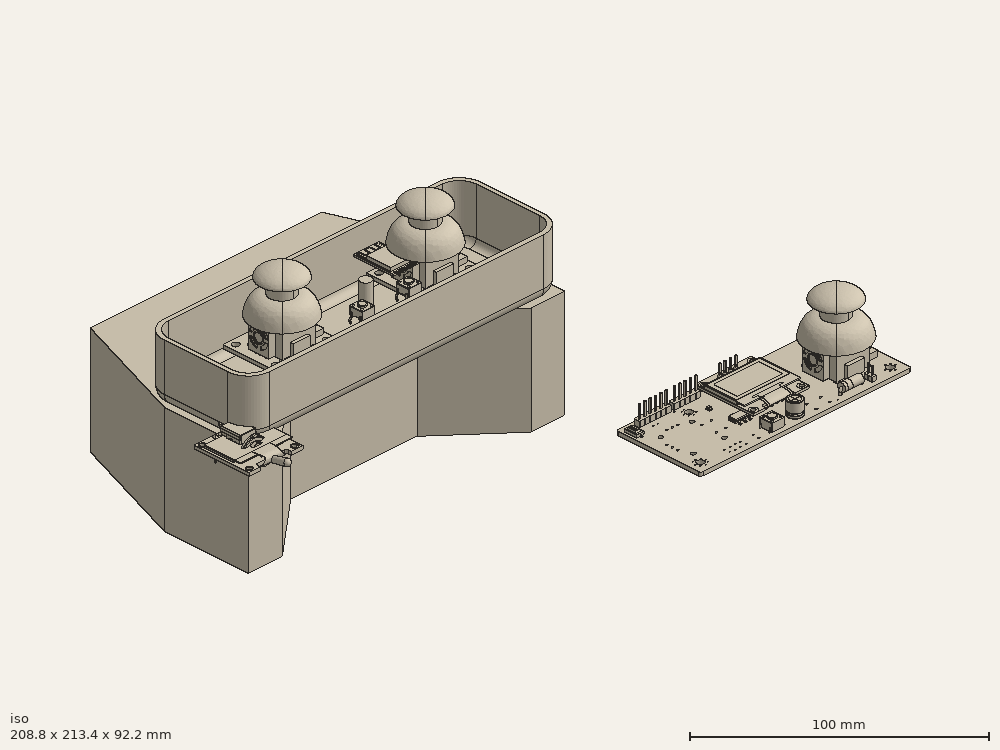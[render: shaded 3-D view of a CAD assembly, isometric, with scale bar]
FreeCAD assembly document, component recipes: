
FREECAD ASSEMBLY — COMPONENT RECIPES ("Transmitter Case V1")

This assembly document has 8 components, labeled P0..P7 below (a component is one placed body or linked part). 4 of them carry a construction recipe — the FreeCAD feature program that regenerates the part from scratch, quoted from this document or its linked companion documents; the rest are supplied as boundary geometry only. No exploded tour is included for this assembly.
COMPONENT P0 — geometry summary ("TransmitterV1"; no construction recipe available for this part):
  bounding box: 100.0 x 40.4 x 40.3 mm
  tessellated surface: 126,652 triangles
  volume: 22622 mm^3 (14% of its bounding box)
COMPONENT P1 — recipe-attached ("Body", modeled in this document).
Construction recipe (the document's own serialized feature program — sketch geometry with constraints, then the solid features built on it; lengths are millimeters unless a unit is written):

FEATURE [Sketcher::SketchObject] Sketch
  FullyConstrained = true
  MapMode = 5
  Support = -> [XY_Plane]
  sketch-geometry (14):
    g0: LineSegment StartX=0 StartY=0 StartZ=0 EndX=0 EndY=40 EndZ=0
    g1: LineSegment StartX=0 StartY=40 StartZ=0 EndX=20 EndY=95 EndZ=0
    g2: LineSegment StartX=20 StartY=95 StartZ=0 EndX=130 EndY=95 EndZ=0
    g3: LineSegment StartX=130 StartY=95 StartZ=0 EndX=150 EndY=40 EndZ=0
    g4: LineSegment StartX=150 StartY=40 StartZ=0 EndX=150 EndY=0 EndZ=0
    g5: LineSegment StartX=150 StartY=0 StartZ=0 EndX=134 EndY=0 EndZ=0
    g6: LineSegment StartX=134 StartY=0 StartZ=0 EndX=105 EndY=25 EndZ=0
    g7: LineSegment StartX=105 StartY=25 StartZ=0 EndX=45 EndY=25 EndZ=0
    g8: LineSegment StartX=45 StartY=25 StartZ=0 EndX=16 EndY=0 EndZ=0
    g9: LineSegment StartX=16 StartY=0 StartZ=0 EndX=0 EndY=0 EndZ=0
    g10: LineSegment StartX=0 StartY=40 StartZ=0 EndX=20 EndY=40 EndZ=0
    g11: LineSegment StartX=150 StartY=40 StartZ=0 EndX=130 EndY=40 EndZ=0
    g12: LineSegment StartX=134 StartY=0 StartZ=0 EndX=105 EndY=0 EndZ=0
    g13: LineSegment StartX=16 StartY=0 StartZ=0 EndX=45 EndY=0 EndZ=0
  constraints (41):
    c: Coincident(g0,g-1)
    c: PointOnObject(g0,g-2)
    c: Coincident(g1,g0)
    c: Horizontal(g2)
    c: Coincident(g4,g3)
    c: Vertical(g4)
    c: Horizontal(g5)
    c: Coincident(g6,g5)
    c: Coincident(g7,g6)
    c: Horizontal(g7)
    c: Coincident(g8,g7)
    c: PointOnObject(g8,g-1)
    c: Coincident(g9,g8)
    c: Coincident(g9,g0)
    c: PointOnObject(g5,g-1)
    c: Equal(g0,g4)
    c: Equal(g8,g6)
    c: Equal(g9,g5)
    c: Equal(g1,g3)
    c: Coincident(g10,g0)
    c: Horizontal(g10)
    c: Coincident(g11,g3)
    c: Horizontal(g11)
    c: Coincident(g12,g5)
    c: Coincident(g13,g8)
    c: Horizontal(g13)
    c: Horizontal(g12)
    c: Vertical(g13,g7)
    c: Vertical(g12,g6)
    c: Distance(g7) = 60
    c: Distance(g3,g1) = 110
    c: Equal(g10,g11)
    c: DistanceY(g0,g2) = 95
    c: Distance(g0,g5) = 150
    c: Coincident(g1,g2)
    c: Coincident(g2,g3)
    c: Vertical(g11,g2)
    c: Coincident(g5,g4)
    c: Distance(g4) = 40
    c: Distance(g5) = 16
    c: Distance(g7,g13) = 25
FEATURE [PartDesign::Pad] Pad
  Direction = (1,1,1)
  Length = 48
  Length2 = 100
  Profile = -> Sketch
  Reversed = true
  Type = 0
FEATURE [Sketcher::SketchObject] Sketch001
  ExternalGeometry = -> [Pad]
  FullyConstrained = true
  MapMode = 5
  Support = -> [Pad]
  sketch-geometry (4):
    g0: LineSegment StartX=0 StartY=-1 StartZ=0 EndX=-63.05 EndY=-1 EndZ=0
    g1: LineSegment StartX=-63.05 StartY=-1 StartZ=0 EndX=-63.05 EndY=98.76 EndZ=0
    g2: LineSegment StartX=-63.05 StartY=98.76 StartZ=0 EndX=0 EndY=98.76 EndZ=0
    g3: LineSegment StartX=0 StartY=98.76 StartZ=0 EndX=0 EndY=-1 EndZ=0
  constraints (12):
    c: Coincident(g0,g1)
    c: Coincident(g1,g2)
    c: Coincident(g2,g3)
    c: Coincident(g3,g0)
    c: Horizontal(g0)
    c: Horizontal(g2)
    c: Vertical(g1)
    c: Vertical(g3)
    c: Distance(g0) = 63.05
    c: Distance(g3) = 99.76
    c: Vertical(g-1,g0)
    c: Distance(g-1,g0) = 1
FEATURE [PartDesign::Body] Body
  Group = -> [Sketch,Pad,Sketch001]
  Origin = -> Origin
  Tip = -> Pad
COMPONENT P2 — recipe-attached ("Body001", modeled in this document).
Construction recipe (the document's own serialized feature program — sketch geometry with constraints, then the solid features built on it; lengths are millimeters unless a unit is written):

FEATURE [Sketcher::SketchObject] Sketch002
  FullyConstrained = true
  MapMode = 5
  Support = -> [XY_Plane001]
  sketch-geometry (16):
    g0: LineSegment StartX=10 StartY=0 StartZ=0 EndX=140 EndY=0 EndZ=0
    g1: LineSegment StartX=150 StartY=10 StartZ=0 EndX=150 EndY=40 EndZ=0
    g2: LineSegment StartX=140 StartY=50 StartZ=0 EndX=10 EndY=50 EndZ=0
    g3: LineSegment StartX=0 StartY=40 StartZ=0 EndX=0 EndY=10 EndZ=0
    g4: LineSegment StartX=0 StartY=0 StartZ=0 EndX=150 EndY=0 EndZ=0
    g5: LineSegment StartX=150 StartY=0 StartZ=0 EndX=150 EndY=50 EndZ=0
    g6: LineSegment StartX=150 StartY=50 StartZ=0 EndX=0 EndY=50 EndZ=0
    g7: LineSegment StartX=0 StartY=50 StartZ=0 EndX=0 EndY=0 EndZ=0
    g8: ArcOfCircle CenterX=140 CenterY=40 CenterZ=0 NormalX=0 NormalY=0 NormalZ=1 AngleXU=0 Radius=10 StartAngle=2e-16 EndAngle=1.5708
    g9: ArcOfCircle CenterX=140 CenterY=10 CenterZ=0 NormalX=0 NormalY=0 NormalZ=1 AngleXU=0 Radius=10 StartAngle=4.71239 EndAngle=6.28319
    g10: ArcOfCircle CenterX=10 CenterY=10 CenterZ=0 NormalX=0 NormalY=0 NormalZ=1 AngleXU=0 Radius=10 StartAngle=3.14159 EndAngle=4.71239
    g11: ArcOfCircle CenterX=10 CenterY=40 CenterZ=0 NormalX=0 NormalY=0 NormalZ=1 AngleXU=0 Radius=10 StartAngle=1.5708 EndAngle=3.14159
    g12: LineSegment StartX=140 StartY=40 StartZ=0 EndX=140 EndY=50 EndZ=0
    g13: LineSegment StartX=140 StartY=10 StartZ=0 EndX=140 EndY=0 EndZ=0
    g14: LineSegment StartX=10 StartY=0 StartZ=0 EndX=10 EndY=10 EndZ=0
    g15: LineSegment StartX=10 StartY=40 StartZ=0 EndX=10 EndY=50 EndZ=0
  constraints (39):
    c: Horizontal(g0)
    c: Vertical(g1)
    c: Vertical(g3)
    c: Coincident(g4,g5)
    c: Coincident(g5,g6)
    c: Coincident(g6,g7)
    c: Coincident(g7,g4)
    c: Horizontal(g4)
    c: Horizontal(g6)
    c: Vertical(g5)
    c: Vertical(g7)
    c: Coincident(g4,g-1)
    c: Distance(g5) = 50
    c: Distance(g4) = 150
    c: Tangent(g2,g8) = -1.5708
    c: Tangent(g1,g8) = -1.5708
    c: Tangent(g1,g9) = -1.5708
    c: Tangent(g0,g9) = -1.5708
    c: Tangent(g0,g10) = -1.5708
    c: Tangent(g3,g10) = -1.5708
    c: Tangent(g2,g11) = -1.5708
    c: Tangent(g3,g11) = -1.5708
    c: PointOnObject(g0,g4)
    c: PointOnObject(g3,g7)
    c: PointOnObject(g2,g6)
    c: PointOnObject(g1,g5)
    c: Coincident(g12,g8)
    c: Coincident(g12,g2)
    c: Vertical(g12)
    c: Coincident(g13,g9)
    c: Coincident(g13,g0)
    c: Coincident(g14,g0)
    c: Coincident(g14,g10)
    c: Coincident(g15,g11)
    c: Coincident(g15,g2)
    c: Equal(g15,g14)
    c: Equal(g14,g12)
    c: Equal(g12,g13)
    c: Distance(g15) = 10
FEATURE [PartDesign::Pad] Pad001
  Direction = (1,1,1)
  Length = 26
  Length2 = 100
  Profile = -> Sketch002
  Type = 0
FEATURE [PartDesign::Fillet] Fillet
  Base = -> Pad001 [Edge3]
  BaseFeature = -> Pad001
  Radius = 5
  SupportTransform = false
FEATURE [PartDesign::Thickness] Thickness
  Base = -> Fillet [Face4]
  BaseFeature = -> Fillet
  Intersection = false
  Join = 0
  Mode = 0
  Reversed = true
  SupportTransform = false
  Value = 2
FEATURE [Sketcher::SketchObject] Sketch010
  ExternalGeometry = -> [Thickness]
  FullyConstrained = true
  MapMode = 5
  Placement = pos=(0,0,2) rot=(0,0,1;0rad)
  Support = -> [Thickness]
  sketch-geometry (4):
    g0: Circle CenterX=52 CenterY=37.5 CenterZ=0 NormalX=0 NormalY=0 NormalZ=1 AngleXU=0 Radius=2.5
    g1: Circle CenterX=92.5 CenterY=36.8 CenterZ=0 NormalX=0 NormalY=0 NormalZ=1 AngleXU=0 Radius=2.5
    g2: Circle CenterX=121 CenterY=11.2 CenterZ=0 NormalX=0 NormalY=0 NormalZ=1 AngleXU=0 Radius=2.5
    g3: Circle CenterX=31 CenterY=11.2 CenterZ=0 NormalX=0 NormalY=0 NormalZ=1 AngleXU=0 Radius=2.5
  constraints (12):
    c: Diameter(g3) = 5
    c: Equal(g3,g0)
    c: Equal(g3,g1)
    c: Equal(g3,g2)
    c: Distance(g3,g-6) = 11.2
    c: Distance(g3,g-4) = 31
    c: Distance(g2,g-6) = 11.2
    c: Distance(g2,g-5) = 29
    c: Distance(g0,g-3) = 12.5
    c: Distance(g0,g-4) = 52
    c: Distance(g1,g-3) = 13.2
    c: Distance(g1,g-5) = 57.5
FEATURE [PartDesign::Pad] Pad004
  BaseFeature = -> Thickness
  Direction = (1,1,1)
  Length = 11
  Length2 = 100
  Profile = -> Sketch010
  Type = 0
FEATURE [Sketcher::SketchObject] Sketch011
  ExternalGeometry = -> [Pad004]
  FullyConstrained = false
  MapMode = 5
  Placement = pos=(-1.1e-14,50,0) rot=(0,0.707107,0.707107;3.14159rad)
  Support = -> [Pad004]
  sketch-geometry (2):
    g0: Circle CenterX=-134.032 CenterY=16.8099 CenterZ=0 NormalX=0 NormalY=0 NormalZ=1 AngleXU=0 Radius=3.5
    g1: Circle CenterX=-15.9615 CenterY=16.8655 CenterZ=0 NormalX=0 NormalY=0 NormalZ=1 AngleXU=0 Radius=3.5
  constraints (4):
    c: Distance(g-4) = 21
    c: Distance(g-4) = 21
    c: Diameter(g0) = 7
    c: Equal(g0,g1)
FEATURE [PartDesign::Body] Body001
  Group = -> [Sketch002,Pad001,Fillet,Thickness,Sketch010,Pad004,Sketch011]
  Origin = -> Origin001
  Tip = -> Pad004
COMPONENT P3 — recipe-attached ("Body002", modeled in this document).
Construction recipe (the document's own serialized feature program — sketch geometry with constraints, then the solid features built on it; lengths are millimeters unless a unit is written):

FEATURE [Sketcher::SketchObject] Sketch003
  FullyConstrained = true
  MapMode = 5
  Support = -> [XY_Plane009]
  sketch-geometry (40):
    g0: LineSegment StartX=0 StartY=0 StartZ=0 EndX=30 EndY=0 EndZ=0
    g1: LineSegment StartX=30 StartY=0 StartZ=0 EndX=30 EndY=25 EndZ=0
    g2: LineSegment StartX=30 StartY=25 StartZ=0 EndX=0 EndY=25 EndZ=0
    g3: LineSegment StartX=0 StartY=25 StartZ=0 EndX=0 EndY=0 EndZ=0
    g4: Circle CenterX=4.4 CenterY=8.5 CenterZ=0 NormalX=0 NormalY=0 NormalZ=1 AngleXU=0 Radius=0.75
    g5: Circle CenterX=4.4 CenterY=11.05 CenterZ=0 NormalX=0 NormalY=0 NormalZ=1 AngleXU=0 Radius=0.75
    g6: Circle CenterX=4.4 CenterY=13.6 CenterZ=0 NormalX=0 NormalY=0 NormalZ=1 AngleXU=0 Radius=0.75
    g7: Circle CenterX=11.4 CenterY=20.6 CenterZ=0 NormalX=0 NormalY=0 NormalZ=1 AngleXU=0 Radius=0.75
    g8: Circle CenterX=13.95 CenterY=20.6 CenterZ=0 NormalX=0 NormalY=0 NormalZ=1 AngleXU=0 Radius=0.75
    g9: Circle CenterX=16.5 CenterY=20.6 CenterZ=0 NormalX=0 NormalY=0 NormalZ=1 AngleXU=0 Radius=0.75
    g10: Circle CenterX=26.4 CenterY=14.65 CenterZ=0 NormalX=0 NormalY=0 NormalZ=1 AngleXU=0 Radius=0.75
    g11: Circle CenterX=26.4 CenterY=7.8 CenterZ=0 NormalX=0 NormalY=0 NormalZ=1 AngleXU=0 Radius=0.75
    g12: Circle CenterX=22.1 CenterY=7.8 CenterZ=0 NormalX=0 NormalY=0 NormalZ=1 AngleXU=0 Radius=0.75
    g13: Circle CenterX=22.1 CenterY=14.65 CenterZ=0 NormalX=0 NormalY=0 NormalZ=1 AngleXU=0 Radius=0.75
    g14: Circle CenterX=6.5 CenterY=3.35 CenterZ=0 NormalX=0 NormalY=0 NormalZ=1 AngleXU=0 Radius=1
    g15: Circle CenterX=6.5 CenterY=18.75 CenterZ=0 NormalX=0 NormalY=0 NormalZ=1 AngleXU=0 Radius=1
    g16: Circle CenterX=21.35 CenterY=3.35 CenterZ=0 NormalX=0 NormalY=0 NormalZ=1 AngleXU=0 Radius=1
    g17: Circle CenterX=21.35 CenterY=18.75 CenterZ=0 NormalX=0 NormalY=0 NormalZ=1 AngleXU=0 Radius=1
    g18: LineSegment StartX=13.95 StartY=20.6 StartZ=0 EndX=13.95 EndY=25 EndZ=0
    g19: LineSegment StartX=16.5 StartY=20.6 StartZ=0 EndX=13.95 EndY=20.6 EndZ=0
    g20: LineSegment StartX=11.4 StartY=20.6 StartZ=0 EndX=13.95 EndY=20.6 EndZ=0
    g21: LineSegment StartX=13.95 StartY=20.6 StartZ=0 EndX=0 EndY=20.6 EndZ=0
    g22: LineSegment StartX=4.4 StartY=11.05 StartZ=0 EndX=0 EndY=11.05 EndZ=0
    g23: LineSegment StartX=4.4 StartY=13.6 StartZ=0 EndX=4.4 EndY=11.05 EndZ=0
    g24: LineSegment StartX=4.4 StartY=11.05 StartZ=0 EndX=4.4 EndY=8.5 EndZ=0
    g25: LineSegment StartX=4.4 StartY=11.05 StartZ=0 EndX=4.4 EndY=25 EndZ=0
    g26: LineSegment StartX=6.5 StartY=3.35 StartZ=0 EndX=0 EndY=3.35 EndZ=0
    g27: LineSegment StartX=6.5 StartY=3.35 StartZ=0 EndX=6.5 EndY=0 EndZ=0
    g28: LineSegment StartX=26.4 StartY=7.8 StartZ=0 EndX=26.4 EndY=0 EndZ=0
    g29: LineSegment StartX=26.4 StartY=7.8 StartZ=0 EndX=30 EndY=7.8 EndZ=0
    g30: LineSegment StartX=6.5 StartY=18.75 StartZ=0 EndX=6.5 EndY=25 EndZ=0
    g31: LineSegment StartX=6.5 StartY=18.75 StartZ=0 EndX=0 EndY=18.75 EndZ=0
    g32: LineSegment StartX=21.35 StartY=18.75 StartZ=0 EndX=21.35 EndY=25 EndZ=0
    g33: LineSegment StartX=21.35 StartY=18.75 StartZ=0 EndX=30 EndY=18.75 EndZ=0
    g34: LineSegment StartX=21.35 StartY=3.35 StartZ=0 EndX=21.35 EndY=0 EndZ=0
    g35: LineSegment StartX=21.35 StartY=3.35 StartZ=0 EndX=30 EndY=3.35 EndZ=0
    g36: LineSegment StartX=26.4 StartY=14.65 StartZ=0 EndX=26.4 EndY=7.8 EndZ=0
    g37: LineSegment StartX=26.4 StartY=7.8 StartZ=0 EndX=22.1 EndY=7.8 EndZ=0
    g38: LineSegment StartX=22.1 StartY=14.65 StartZ=0 EndX=22.1 EndY=7.8 EndZ=0
    g39: LineSegment StartX=26.4 StartY=14.65 StartZ=0 EndX=22.1 EndY=14.65 EndZ=0
  constraints (111):
    c: Coincident(g0,g1)
    c: Coincident(g1,g2)
    c: Coincident(g2,g3)
    c: Coincident(g3,g0)
    c: Horizontal(g0)
    c: Horizontal(g2)
    c: Vertical(g1)
    c: Vertical(g3)
    c: Coincident(g0,g-1)
    c: Distance(g2) = 30
    c: Distance(g1) = 25
    c: Diameter(g4) = 1.5
    c: Equal(g4,g5) = 1.5
    c: Equal(g4,g6) = 1.5
    c: Equal(g4,g7) = 1.5
    c: Equal(g4,g8) = 1.5
    c: Equal(g4,g9) = 1.5
    c: Equal(g4,g10) = 1.5
    c: Equal(g4,g11) = 1.5
    c: Equal(g4,g12) = 1.5
    c: Diameter(g14) = 2
    c: Equal(g14,g15) = 2
    c: Equal(g14,g16) = 2
    c: Equal(g14,g17) = 2
    c: Coincident(g18,g8)
    c: Vertical(g18)
    c: Coincident(g19,g9)
    c: Coincident(g19,g8)
    c: Horizontal(g19)
    c: Coincident(g20,g7)
    c: Coincident(g20,g8)
    c: Horizontal(g20)
    c: Equal(g20,g19)
    c: Distance(g18) = 4.4
    c: Coincident(g21,g8)
    c: PointOnObject(g21,g3)
    c: Horizontal(g21)
    c: PointOnObject(g18,g2)
    c: Distance(g21) = 13.95
    c: Distance(g20) = 2.55
    c: Coincident(g22,g5)
    c: PointOnObject(g22,g-2)
    c: Horizontal(g22)
    c: Coincident(g23,g6)
    c: Coincident(g23,g5)
    c: Vertical(g23)
    c: Coincident(g24,g5)
    c: Coincident(g24,g4)
    c: Vertical(g24)
    c: Equal(g24,g23)
    c: Distance(g22) = 4.4
    c: Coincident(g25,g5)
    c: PointOnObject(g25,g2)
    c: Vertical(g25)
    c: Distance(g25) = 13.95
    c: Distance(g24) = 2.55
    c: Coincident(g26,g14)
    c: PointOnObject(g26,g-2)
    c: Horizontal(g26)
    c: Coincident(g27,g14)
    c: PointOnObject(g27,g0)
    c: Vertical(g27)
    c: Coincident(g28,g11)
    c: PointOnObject(g28,g0)
    c: Vertical(g28)
    c: Coincident(g29,g11)
    c: Horizontal(g29)
    c: Coincident(g30,g15)
    c: PointOnObject(g30,g2)
    c: Vertical(g30)
    c: Coincident(g31,g15)
    c: PointOnObject(g31,g3)
    c: Horizontal(g31)
    c: Coincident(g32,g17)
    c: PointOnObject(g32,g2)
    c: Vertical(g32)
    c: Coincident(g33,g17)
    c: PointOnObject(g33,g1)
    c: Horizontal(g33)
    c: Coincident(g34,g16)
    c: PointOnObject(g34,g0)
    c: Vertical(g34)
    c: Coincident(g35,g16)
    c: PointOnObject(g35,g1)
    c: Horizontal(g35)
    c: Coincident(g36,g10)
    c: Coincident(g36,g11)
    c: Vertical(g36)
    c: Coincident(g37,g11)
    c: Coincident(g37,g12)
    c: Horizontal(g37)
    c: Coincident(g38,g13)
    c: Coincident(g38,g12)
    c: Vertical(g38)
    c: Coincident(g39,g10)
    c: Coincident(g39,g13)
    c: Horizontal(g39)
    c: Distance(g29) = 3.6
    c: Distance(g37) = 4.3
    c: Distance(g38) = 6.85
    c: Distance(g28) = 7.8
    c: PointOnObject(g29,g1)
    c: Equal(g13,g12)
    c: Distance(g31) = 6.5
    c: Distance(g30) = 6.25
    c: Distance(g32) = 6.25
    c: Distance(g33) = 8.65
    c: Distance(g35) = 8.65
    c: Distance(g34) = 3.35
    c: Distance(g27) = 3.35
    c: Distance(g26) = 6.5
FEATURE [PartDesign::Pad] Pad002
  Direction = (1,1,1)
  Length = 1.6
  Length2 = 100
  Profile = -> Sketch003
  Type = 0
FEATURE [Sketcher::SketchObject] Sketch004
  ExternalGeometry = -> [Pad002]
  FullyConstrained = true
  MapMode = 5
  Placement = pos=(0,0,1.6) rot=(0,0,1;0rad)
  Support = -> [Pad002]
  sketch-geometry (4):
    g0: Circle CenterX=27 CenterY=22 CenterZ=0 NormalX=0 NormalY=0 NormalZ=1 AngleXU=0 Radius=1.55
    g1: Circle CenterX=3 CenterY=22 CenterZ=0 NormalX=0 NormalY=0 NormalZ=1 AngleXU=0 Radius=1.55
    g2: Circle CenterX=27 CenterY=3 CenterZ=0 NormalX=0 NormalY=0 NormalZ=1 AngleXU=0 Radius=1.55
    g3: Circle CenterX=3 CenterY=3 CenterZ=0 NormalX=0 NormalY=0 NormalZ=1 AngleXU=0 Radius=1.55
  constraints (12):
    c: Diameter(g0) = 3.1
    c: Equal(g0,g1) = 3.1
    c: Equal(g0,g2) = 3.1
    c: Equal(g0,g3) = 3.1
    c: Distance(g2,g-5) = 3
    c: Distance(g2,g-6) = 3
    c: Distance(g0,g-3) = 3
    c: Distance(g0,g-5) = 3
    c: Distance(g1,g-3) = 3
    c: Distance(g1,g-4) = 3
    c: Distance(g3,g-4) = 3
    c: Distance(g3,g-6) = 3
FEATURE [PartDesign::Pocket] Pocket
  BaseFeature = -> Pad002
  Length = 5
  Length2 = 100
  Profile = -> Sketch004
  Type = 0
FEATURE [Sketcher::SketchObject] Sketch008
  FullyConstrained = true
  MapMode = 5
  Support = -> [XY_Plane009]
FEATURE [Sketcher::SketchObject] Sketch009
  FullyConstrained = true
  MapMode = 5
  Support = -> [XY_Plane009]
FEATURE [PartDesign::Body] Body002
  Group = -> [Sketch003,Pad002,Sketch004,Pocket,Sketch008,Sketch009]
  Origin = -> Origin009
  Placement = pos=(27,14,12) rot=(0,0,1;0rad)
  Tip = -> Pocket
COMPONENT P4 — recipe-attached ("Body003", modeled in this document).
Construction recipe (the document's own serialized feature program — sketch geometry with constraints, then the solid features built on it; lengths are millimeters unless a unit is written):

FEATURE [Sketcher::SketchObject] Sketch006
  FullyConstrained = true
  MapMode = 5
  Support = -> [XY_Plane010]
  sketch-geometry (40):
    g0: LineSegment StartX=0 StartY=0 StartZ=0 EndX=30 EndY=0 EndZ=0
    g1: LineSegment StartX=30 StartY=0 StartZ=0 EndX=30 EndY=25 EndZ=0
    g2: LineSegment StartX=30 StartY=25 StartZ=0 EndX=0 EndY=25 EndZ=0
    g3: LineSegment StartX=0 StartY=25 StartZ=0 EndX=0 EndY=0 EndZ=0
    g4: Circle CenterX=4.4 CenterY=8.5 CenterZ=0 NormalX=0 NormalY=0 NormalZ=1 AngleXU=0 Radius=0.75
    g5: Circle CenterX=4.4 CenterY=11.05 CenterZ=0 NormalX=0 NormalY=0 NormalZ=1 AngleXU=0 Radius=0.75
    g6: Circle CenterX=4.4 CenterY=13.6 CenterZ=0 NormalX=0 NormalY=0 NormalZ=1 AngleXU=0 Radius=0.75
    g7: Circle CenterX=11.4 CenterY=20.6 CenterZ=0 NormalX=0 NormalY=0 NormalZ=1 AngleXU=0 Radius=0.75
    g8: Circle CenterX=13.95 CenterY=20.6 CenterZ=0 NormalX=0 NormalY=0 NormalZ=1 AngleXU=0 Radius=0.75
    g9: Circle CenterX=16.5 CenterY=20.6 CenterZ=0 NormalX=0 NormalY=0 NormalZ=1 AngleXU=0 Radius=0.75
    g10: Circle CenterX=26.4 CenterY=14.65 CenterZ=0 NormalX=0 NormalY=0 NormalZ=1 AngleXU=0 Radius=0.75
    g11: Circle CenterX=26.4 CenterY=7.8 CenterZ=0 NormalX=0 NormalY=0 NormalZ=1 AngleXU=0 Radius=0.75
    g12: Circle CenterX=22.1 CenterY=7.8 CenterZ=0 NormalX=0 NormalY=0 NormalZ=1 AngleXU=0 Radius=0.75
    g13: Circle CenterX=22.1 CenterY=14.65 CenterZ=0 NormalX=0 NormalY=0 NormalZ=1 AngleXU=0 Radius=0.75
    g14: Circle CenterX=6.5 CenterY=3.35 CenterZ=0 NormalX=0 NormalY=0 NormalZ=1 AngleXU=0 Radius=1
    g15: Circle CenterX=6.5 CenterY=18.75 CenterZ=0 NormalX=0 NormalY=0 NormalZ=1 AngleXU=0 Radius=1
    g16: Circle CenterX=21.35 CenterY=3.35 CenterZ=0 NormalX=0 NormalY=0 NormalZ=1 AngleXU=0 Radius=1
    g17: Circle CenterX=21.35 CenterY=18.75 CenterZ=0 NormalX=0 NormalY=0 NormalZ=1 AngleXU=0 Radius=1
    g18: LineSegment StartX=13.95 StartY=20.6 StartZ=0 EndX=13.95 EndY=25 EndZ=0
    g19: LineSegment StartX=16.5 StartY=20.6 StartZ=0 EndX=13.95 EndY=20.6 EndZ=0
    g20: LineSegment StartX=11.4 StartY=20.6 StartZ=0 EndX=13.95 EndY=20.6 EndZ=0
    g21: LineSegment StartX=13.95 StartY=20.6 StartZ=0 EndX=0 EndY=20.6 EndZ=0
    g22: LineSegment StartX=4.4 StartY=11.05 StartZ=0 EndX=0 EndY=11.05 EndZ=0
    g23: LineSegment StartX=4.4 StartY=13.6 StartZ=0 EndX=4.4 EndY=11.05 EndZ=0
    g24: LineSegment StartX=4.4 StartY=11.05 StartZ=0 EndX=4.4 EndY=8.5 EndZ=0
    g25: LineSegment StartX=4.4 StartY=11.05 StartZ=0 EndX=4.4 EndY=25 EndZ=0
    g26: LineSegment StartX=6.5 StartY=3.35 StartZ=0 EndX=0 EndY=3.35 EndZ=0
    g27: LineSegment StartX=6.5 StartY=3.35 StartZ=0 EndX=6.5 EndY=0 EndZ=0
    g28: LineSegment StartX=26.4 StartY=7.8 StartZ=0 EndX=26.4 EndY=0 EndZ=0
    g29: LineSegment StartX=26.4 StartY=7.8 StartZ=0 EndX=30 EndY=7.8 EndZ=0
    g30: LineSegment StartX=6.5 StartY=18.75 StartZ=0 EndX=6.5 EndY=25 EndZ=0
    g31: LineSegment StartX=6.5 StartY=18.75 StartZ=0 EndX=0 EndY=18.75 EndZ=0
    g32: LineSegment StartX=21.35 StartY=18.75 StartZ=0 EndX=21.35 EndY=25 EndZ=0
    g33: LineSegment StartX=21.35 StartY=18.75 StartZ=0 EndX=30 EndY=18.75 EndZ=0
    g34: LineSegment StartX=21.35 StartY=3.35 StartZ=0 EndX=21.35 EndY=0 EndZ=0
    g35: LineSegment StartX=21.35 StartY=3.35 StartZ=0 EndX=30 EndY=3.35 EndZ=0
    g36: LineSegment StartX=26.4 StartY=14.65 StartZ=0 EndX=26.4 EndY=7.8 EndZ=0
    g37: LineSegment StartX=26.4 StartY=7.8 StartZ=0 EndX=22.1 EndY=7.8 EndZ=0
    g38: LineSegment StartX=22.1 StartY=14.65 StartZ=0 EndX=22.1 EndY=7.8 EndZ=0
    g39: LineSegment StartX=26.4 StartY=14.65 StartZ=0 EndX=22.1 EndY=14.65 EndZ=0
  constraints (111):
    c: Coincident(g0,g1)
    c: Coincident(g1,g2)
    c: Coincident(g2,g3)
    c: Coincident(g3,g0)
    c: Horizontal(g0)
    c: Horizontal(g2)
    c: Vertical(g1)
    c: Vertical(g3)
    c: Coincident(g0,g-1)
    c: Distance(g2) = 30
    c: Distance(g1) = 25
    c: Diameter(g4) = 1.5
    c: Equal(g4,g5) = 1.5
    c: Equal(g4,g6) = 1.5
    c: Equal(g4,g7) = 1.5
    c: Equal(g4,g8) = 1.5
    c: Equal(g4,g9) = 1.5
    c: Equal(g4,g10) = 1.5
    c: Equal(g4,g11) = 1.5
    c: Equal(g4,g12) = 1.5
    c: Diameter(g14) = 2
    c: Equal(g14,g15) = 2
    c: Equal(g14,g16) = 2
    c: Equal(g14,g17) = 2
    c: Coincident(g18,g8)
    c: Vertical(g18)
    c: Coincident(g19,g9)
    c: Coincident(g19,g8)
    c: Horizontal(g19)
    c: Coincident(g20,g7)
    c: Coincident(g20,g8)
    c: Horizontal(g20)
    c: Equal(g20,g19)
    c: Distance(g18) = 4.4
    c: Coincident(g21,g8)
    c: PointOnObject(g21,g3)
    c: Horizontal(g21)
    c: PointOnObject(g18,g2)
    c: Distance(g21) = 13.95
    c: Distance(g20) = 2.55
    c: Coincident(g22,g5)
    c: PointOnObject(g22,g-2)
    c: Horizontal(g22)
    c: Coincident(g23,g6)
    c: Coincident(g23,g5)
    c: Vertical(g23)
    c: Coincident(g24,g5)
    c: Coincident(g24,g4)
    c: Vertical(g24)
    c: Equal(g24,g23)
    c: Distance(g22) = 4.4
    c: Coincident(g25,g5)
    c: PointOnObject(g25,g2)
    c: Vertical(g25)
    c: Distance(g25) = 13.95
    c: Distance(g24) = 2.55
    c: Coincident(g26,g14)
    c: PointOnObject(g26,g-2)
    c: Horizontal(g26)
    c: Coincident(g27,g14)
    c: PointOnObject(g27,g0)
    c: Vertical(g27)
    c: Coincident(g28,g11)
    c: PointOnObject(g28,g0)
    c: Vertical(g28)
    c: Coincident(g29,g11)
    c: Horizontal(g29)
    c: Coincident(g30,g15)
    c: PointOnObject(g30,g2)
    c: Vertical(g30)
    c: Coincident(g31,g15)
    c: PointOnObject(g31,g3)
    c: Horizontal(g31)
    c: Coincident(g32,g17)
    c: PointOnObject(g32,g2)
    c: Vertical(g32)
    c: Coincident(g33,g17)
    c: PointOnObject(g33,g1)
    c: Horizontal(g33)
    c: Coincident(g34,g16)
    c: PointOnObject(g34,g0)
    c: Vertical(g34)
    c: Coincident(g35,g16)
    c: PointOnObject(g35,g1)
    c: Horizontal(g35)
    c: Coincident(g36,g10)
    c: Coincident(g36,g11)
    c: Vertical(g36)
    c: Coincident(g37,g11)
    c: Coincident(g37,g12)
    c: Horizontal(g37)
    c: Coincident(g38,g13)
    c: Coincident(g38,g12)
    c: Vertical(g38)
    c: Coincident(g39,g10)
    c: Coincident(g39,g13)
    c: Horizontal(g39)
    c: Distance(g29) = 3.6
    c: Distance(g37) = 4.3
    c: Distance(g38) = 6.85
    c: Distance(g28) = 7.8
    c: PointOnObject(g29,g1)
    c: Equal(g13,g12)
    c: Distance(g31) = 6.5
    c: Distance(g30) = 6.25
    c: Distance(g32) = 6.25
    c: Distance(g33) = 8.65
    c: Distance(g35) = 8.65
    c: Distance(g34) = 3.35
    c: Distance(g27) = 3.35
    c: Distance(g26) = 6.5
FEATURE [PartDesign::Pad] Pad003
  Direction = (1,1,1)
  Length = 1.6
  Length2 = 100
  Profile = -> Sketch006
  Type = 0
FEATURE [Sketcher::SketchObject] Sketch005
  ExternalGeometry = -> [Pad003]
  FullyConstrained = true
  MapMode = 5
  Placement = pos=(0,0,1.6) rot=(0,0,1;0rad)
  Support = -> [Pad003]
  sketch-geometry (4):
    g0: Circle CenterX=27 CenterY=22 CenterZ=0 NormalX=0 NormalY=0 NormalZ=1 AngleXU=0 Radius=1.55
    g1: Circle CenterX=3 CenterY=22 CenterZ=0 NormalX=0 NormalY=0 NormalZ=1 AngleXU=0 Radius=1.55
    g2: Circle CenterX=27 CenterY=3 CenterZ=0 NormalX=0 NormalY=0 NormalZ=1 AngleXU=0 Radius=1.55
    g3: Circle CenterX=3 CenterY=3 CenterZ=0 NormalX=0 NormalY=0 NormalZ=1 AngleXU=0 Radius=1.55
  constraints (12):
    c: Diameter(g0) = 3.1
    c: Equal(g0,g1) = 3.1
    c: Equal(g0,g2) = 3.1
    c: Equal(g0,g3) = 3.1
    c: Distance(g2,g-5) = 3
    c: Distance(g2,g-6) = 3
    c: Distance(g0,g-3) = 3
    c: Distance(g0,g-5) = 3
    c: Distance(g1,g-3) = 3
    c: Distance(g1,g-4) = 3
    c: Distance(g3,g-4) = 3
    c: Distance(g3,g-6) = 3
FEATURE [PartDesign::Pocket] Pocket001
  BaseFeature = -> Pad003
  Length = 5
  Length2 = 100
  Profile = -> Sketch005
  Type = 0
FEATURE [PartDesign::Body] Body003
  Group = -> [Sketch006,Pad003,Sketch005,Pocket001]
  Origin = -> Origin010
  Placement = pos=(95,14,12) rot=(0,0,1;0rad)
  Tip = -> Pocket001
COMPONENT P5 — geometry summary ("MTS-1xx-X002"; no construction recipe available for this part):
  bounding box: 33.3 x 13.4 x 12.0 mm
  tessellated surface: 85,122 triangles
  volume: 1067 mm^3 (20% of its bounding box)
COMPONENT P6 — geometry summary ("MTS-1xx-X1"; no construction recipe available for this part):
  bounding box: 33.3 x 13.4 x 12.0 mm
  tessellated surface: 85,122 triangles
  volume: 1067 mm^3 (20% of its bounding box)
COMPONENT P7 — geometry summary ("SSD1306_OLED_Display(128x64) v23"; no construction recipe available for this part):
  bounding box: 26.2 x 25.4 x 11.8 mm
  tessellated surface: 21,990 triangles
  volume: 1607 mm^3 (20% of its bounding box)
PROVENANCE & LICENSES
A FreeCAD (.FCStd) document from a public repository crawl; recipes are the document's own serialized feature recipes (and, for linked parts, companion documents' recipes).
License: apache-2.0.
